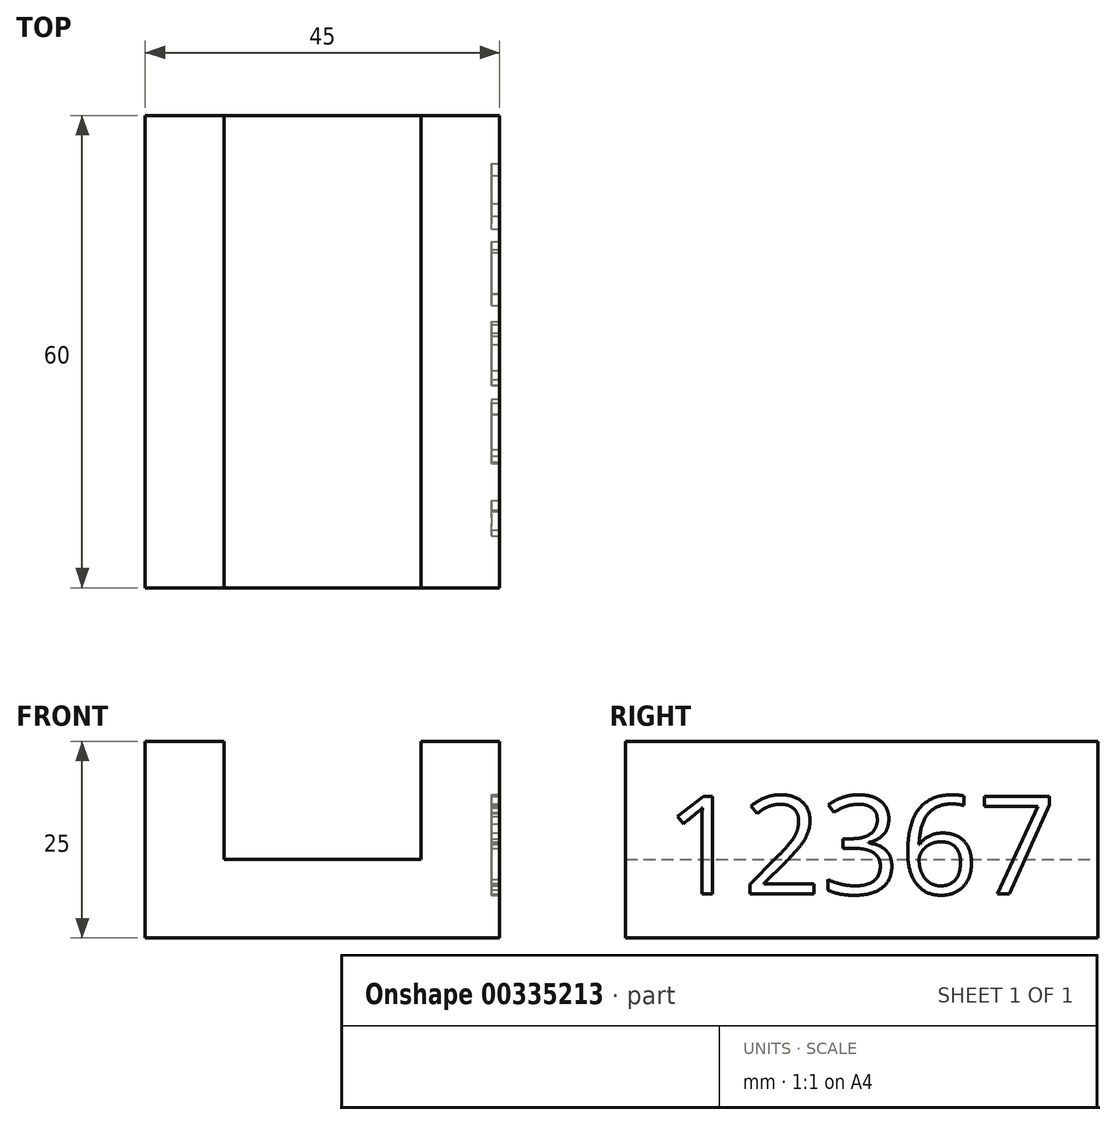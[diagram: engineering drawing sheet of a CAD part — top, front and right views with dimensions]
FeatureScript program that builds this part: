
annotation { "Feature Type Name" : "Feature", "Feature Type Description" : "" }
export const myFeature = defineFeature(function(context is Context, id is Id, definition is map)
    precondition{}
    {
        {
            var Q0;
            Q0=qCreatedBy(makeId("Front.planeOp"),FACE);
            var sketch = newSketch(context, id + "F0", { "sketchPlane" : qUnion([Q0])});
            skLineSegment(sketch, "E0.bottom", {"start": v(22.5, -10) * mm, "end": v(-22.5, -10) * mm});
            skLineSegment(sketch, "E0.top", {"start": v(22.5, 15) * mm, "end": v(-22.5, 15) * mm});
            skLineSegment(sketch, "E0.left", {"start": v(22.5, -10) * mm, "end": v(22.5, 15) * mm});
            skLineSegment(sketch, "E0.right", {"start": v(-22.5, -10) * mm, "end": v(-22.5, 15) * mm});
            skPoint(sketch, "E0.middle", {"position": v(0, 2.5) * mm});
            skLineSegment(sketch, "E1.bottom", {"start": v(12.5, 0) * mm, "end": v(-12.5, 0) * mm});
            skLineSegment(sketch, "E1.top", {"start": v(12.5, 30) * mm, "end": v(-12.5, 30) * mm});
            skLineSegment(sketch, "E1.left", {"start": v(12.5, 0) * mm, "end": v(12.5, 30) * mm});
            skLineSegment(sketch, "E1.right", {"start": v(-12.5, 0) * mm, "end": v(-12.5, 30) * mm});
            skPoint(sketch, "E1.middle", {"position": v(0, 15) * mm});
            skSolve(sketch);
        }
        {
            var Q0;
            Q0=makeQuery(id+"F0.imprint","IMPRINT",FACE,{"disambiguationData":[TD([[makeQuery(id+"F0.imprint","IMPRINT",EDGE,{"derivedFrom":sQuery(id+"F0.wireOp",EDGE,"E0.bottom")}),-1.0]])]});
            extrude(context, id + "F1", {"entities" : qUnion([Q0]), "depth" : 60 * mm});
        }
        {
            var Q0;
            Q0=makeQuery(id+"F1.opExtrude","SWEPT_FACE",FACE,{"disambiguationData":[OSD([sQuery(id+"F0.wireOp",EDGE,"E0.left")])]});
            var sketch = newSketch(context, id + "F2", { "sketchPlane" : qUnion([Q0])});
            skText(sketch, "E2", { "text": "12367", "fontName": "OpenSans-Regular.ttf"});
            const initialGuessF2  = {"E2": [-0.055, -0.0044, 1, 0, 0.01253]};
            skSetInitialGuess(sketch, initialGuessF2);
            skSolve(sketch);
        }
        {
            var Q0;
            Q0 = qSketchRegion(id + "F2", true);
            extrude(context, id + "F3", {"entities" : qUnion([Q0]), "operationType" : NewBodyOperationType.REMOVE, "oppositeDirection" : true, "depth" : 1 * mm});
        }
    });
